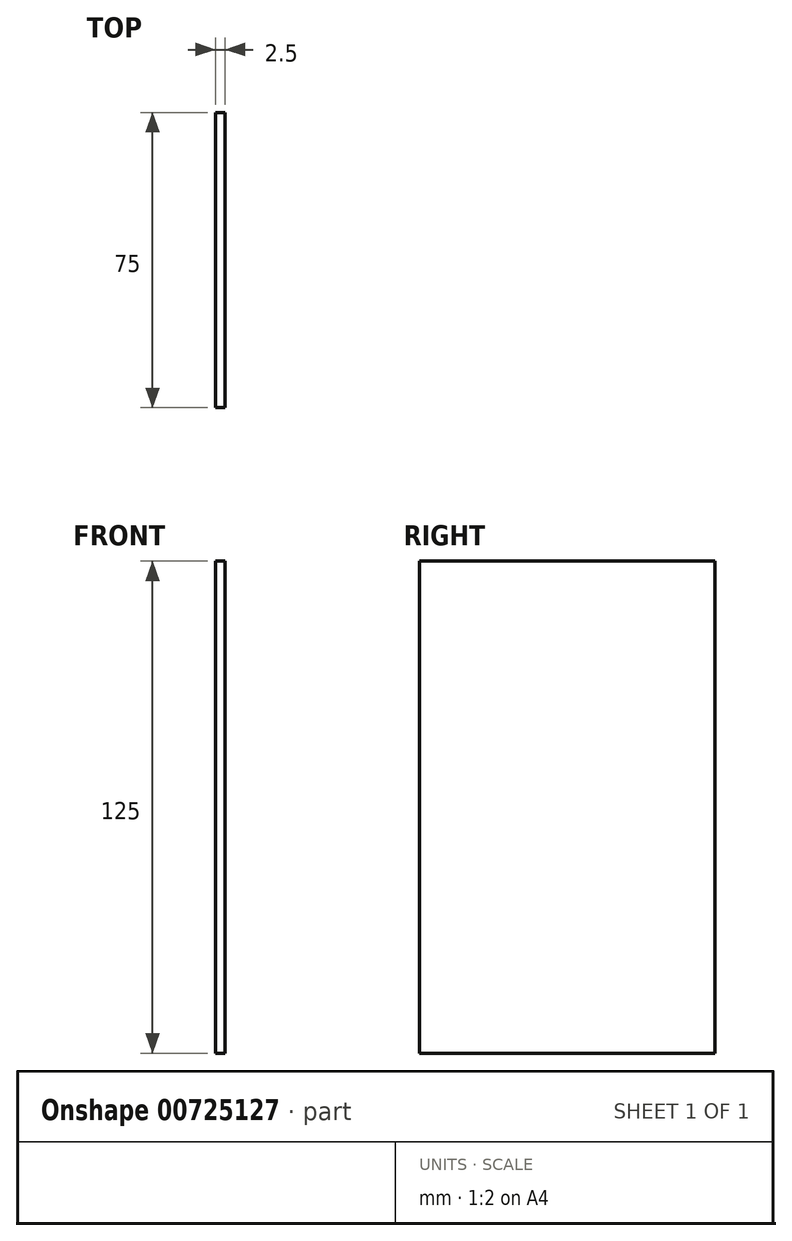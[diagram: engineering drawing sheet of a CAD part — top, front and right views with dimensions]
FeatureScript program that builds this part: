
annotation { "Feature Type Name" : "Feature", "Feature Type Description" : "" }
export const myFeature = defineFeature(function(context is Context, id is Id, definition is map)
    precondition{}
    {
        {
            var Q0;
            Q0=qCreatedBy(makeId("Right.planeOp"),FACE);
            var sketch = newSketch(context, id + "F0", { "sketchPlane" : qUnion([Q0])});
            skLineSegment(sketch, "E0.bottom", {"start": v(-49.98, -45.91) * mm, "end": v(25.02, -45.91) * mm});
            skLineSegment(sketch, "E0.top", {"start": v(-49.98, 79.09) * mm, "end": v(25.02, 79.09) * mm});
            skLineSegment(sketch, "E0.left", {"start": v(-49.98, -45.91) * mm, "end": v(-49.98, 79.09) * mm});
            skLineSegment(sketch, "E0.right", {"start": v(25.02, -45.91) * mm, "end": v(25.02, 79.09) * mm});
            skSolve(sketch);
        }
        {
            var Q0;
            Q0 = qSketchRegion(id + "F0", true);
            extrude(context, id + "F1", {"entities" : qUnion([Q0]), "depth" : 2.5 * mm, "offsetDistance" : 25.4 * mm});
        }
    });
